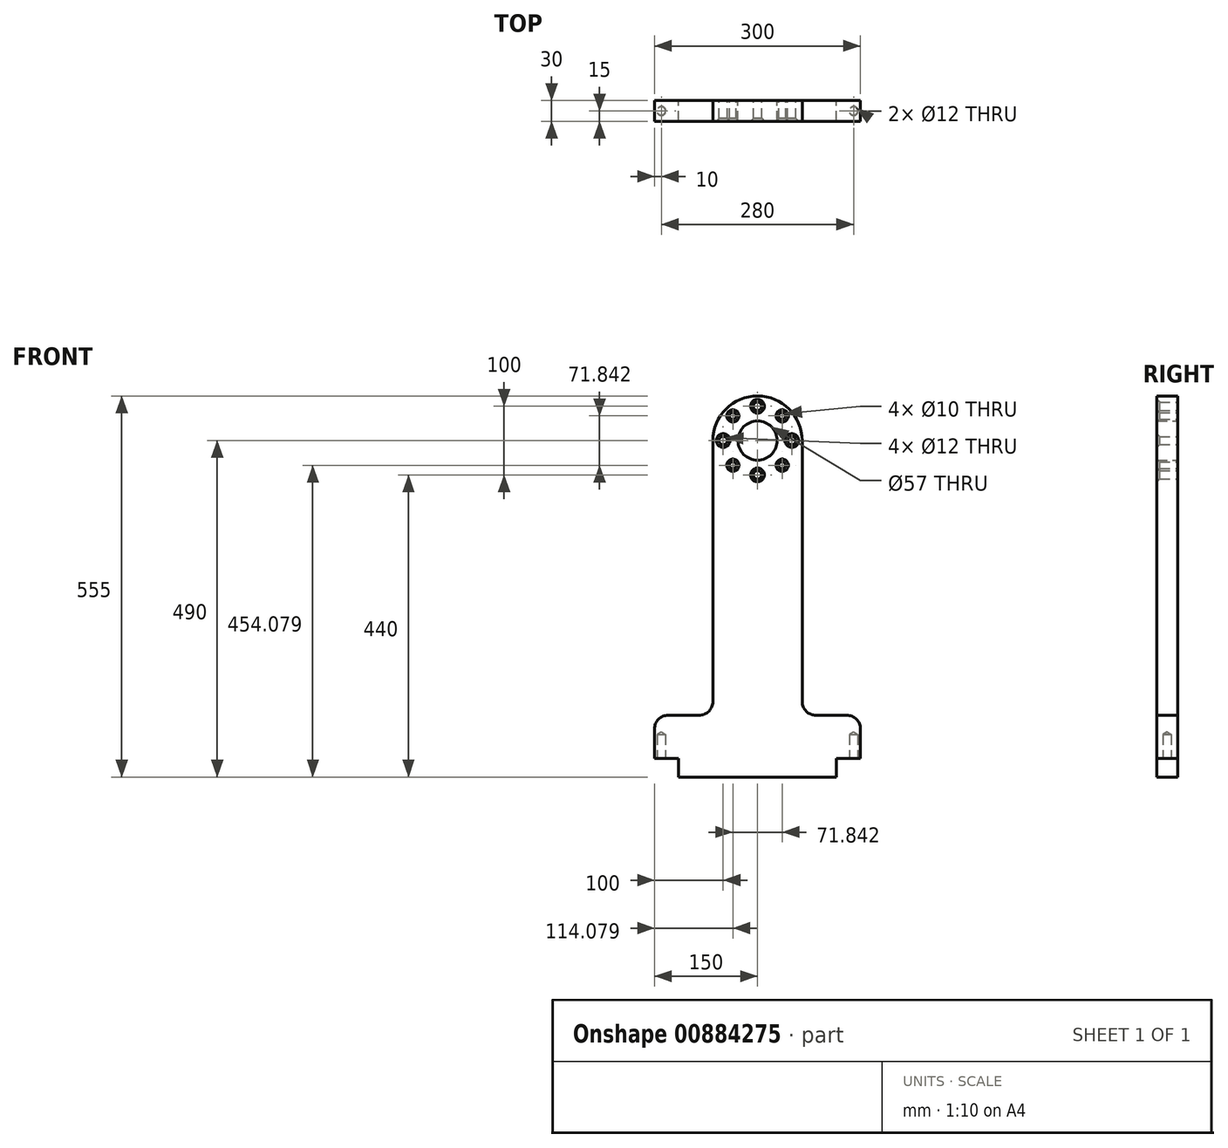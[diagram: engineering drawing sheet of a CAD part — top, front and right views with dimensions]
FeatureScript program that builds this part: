
annotation { "Feature Type Name" : "Feature", "Feature Type Description" : "" }
export const myFeature = defineFeature(function(context is Context, id is Id, definition is map)
    precondition{}
    {
        {
            var Q0;
            Q0=qCreatedBy(makeId("Front.planeOp"),FACE);
            var sketch = newSketch(context, id + "F0", { "sketchPlane" : qUnion([Q0])});
            skLineSegment(sketch, "E0", {"start": v(0, 65) * mm, "end": v(0, 65) * mm});
            skLineSegment(sketch, "E1", {"start": v(65, 0) * mm, "end": v(65, -380) * mm});
            skLineSegment(sketch, "E2", {"start": v(85, -400) * mm, "end": v(130, -400) * mm});
            skLineSegment(sketch, "E3", {"start": v(150, -420) * mm, "end": v(150, -490) * mm});
            skLineSegment(sketch, "E4", {"start": v(150, -490) * mm, "end": v(-150, -490) * mm});
            skLineSegment(sketch, "E5", {"start": v(-150, -490) * mm, "end": v(-150, -420) * mm});
            skLineSegment(sketch, "E6", {"start": v(-130, -400) * mm, "end": v(-85, -400) * mm});
            skLineSegment(sketch, "E7", {"start": v(-65, -380) * mm, "end": v(-65, 0) * mm});
            skPoint(sketch, "E8.visualSharp", {"position": v(-65, 65) * mm});
            skArc(sketch, "E8.filletArc", {"start": v(0, 65) * mm, "mid": v(-45.96, 45.96) * mm, "end": v(-65, 0) * mm});
            skPoint(sketch, "E9.visualSharp", {"position": v(65, 65) * mm});
            skArc(sketch, "E9.filletArc", {"start": v(65, 0) * mm, "mid": v(45.96, 45.96) * mm, "end": v(0, 65) * mm});
            skPoint(sketch, "E10.visualSharp", {"position": v(-65, -400) * mm});
            skArc(sketch, "E10.filletArc", {"start": v(-85, -400) * mm, "mid": v(-70.86, -394.14) * mm, "end": v(-65, -380) * mm});
            skPoint(sketch, "E11.visualSharp", {"position": v(65, -400) * mm});
            skArc(sketch, "E11.filletArc", {"start": v(65, -380) * mm, "mid": v(70.86, -394.14) * mm, "end": v(85, -400) * mm});
            skPoint(sketch, "E12.visualSharp", {"position": v(-150, -400) * mm});
            skArc(sketch, "E12.filletArc", {"start": v(-130, -400) * mm, "mid": v(-144.14, -405.86) * mm, "end": v(-150, -420) * mm});
            skPoint(sketch, "E13.visualSharp", {"position": v(150, -400) * mm});
            skArc(sketch, "E13.filletArc", {"start": v(150, -420) * mm, "mid": v(144.14, -405.86) * mm, "end": v(130, -400) * mm});
            skCircle(sketch, "E14", {"center": v(0, 0) * mm, "radius": 28.5 * mm});
            skCircle(sketch, "E15", {"center": v(0, 50) * mm, "radius": 6 * mm});
            skCircle(sketch, "E16.1.0", {"center": v(-50, 0) * mm, "radius": 6 * mm});
            skCircle(sketch, "E16.2.0", {"center": v(0, -50) * mm, "radius": 6 * mm});
            skCircle(sketch, "E16.3.0", {"center": v(50, 0) * mm, "radius": 6 * mm});
            skCircle(sketch, "E17", {"center": v(-35.92, 35.92) * mm, "radius": 5 * mm});
            skLineSegment(sketch, "E18", {"start": v(-35.92, 35.92) * mm, "end": v(0, 0) * mm, "construction": true});
            skCircle(sketch, "E19.1.0", {"center": v(-35.92, -35.92) * mm, "radius": 5 * mm});
            skCircle(sketch, "E19.2.0", {"center": v(35.92, -35.92) * mm, "radius": 5 * mm});
            skCircle(sketch, "E19.3.0", {"center": v(35.92, 35.92) * mm, "radius": 5 * mm});
            skLineSegment(sketch, "E20.bottom", {"start": v(150, -463) * mm, "end": v(115, -463) * mm});
            skLineSegment(sketch, "E20.top", {"start": v(150, -490) * mm, "end": v(115, -490) * mm});
            skLineSegment(sketch, "E20.left", {"start": v(150, -463) * mm, "end": v(150, -490) * mm});
            skLineSegment(sketch, "E20.right", {"start": v(115, -463) * mm, "end": v(115, -490) * mm});
            skLineSegment(sketch, "E21.bottom", {"start": v(-150, -463) * mm, "end": v(-115, -463) * mm});
            skLineSegment(sketch, "E21.top", {"start": v(-150, -490) * mm, "end": v(-115, -490) * mm});
            skLineSegment(sketch, "E21.left", {"start": v(-150, -463) * mm, "end": v(-150, -490) * mm});
            skLineSegment(sketch, "E21.right", {"start": v(-115, -463) * mm, "end": v(-115, -490) * mm});
            skSolve(sketch);
        }
        {
            var Q0;
            Q0=makeQuery(id+"F0.imprint","IMPRINT",FACE,{"disambiguationData":[TD([[makeQuery(id+"F0.imprint","IMPRINT",EDGE,{"derivedFrom":sQuery(id+"F0.wireOp",EDGE,"E1")}),-1.0]])]});
            extrude(context, id + "F1", {"entities" : qUnion([Q0]), "depth" : 30 * mm, "offsetDistance" : 25 * mm});
        }
        {
            var Q0;
            Q0=makeQuery(id+"F1.opExtrude","CAP_EDGE",EDGE,{"disambiguationData":[OSD([sQuery(id+"F0.wireOp",EDGE,"E17")])],"isStart":false});
            var Q1;
            Q1=makeQuery(id+"F1.opExtrude","CAP_EDGE",EDGE,{"disambiguationData":[OSD([sQuery(id+"F0.wireOp",EDGE,"E15")])],"isStart":false});
            var Q2;
            Q2=makeQuery(id+"F1.opExtrude","CAP_EDGE",EDGE,{"disambiguationData":[OSD([sQuery(id+"F0.wireOp",EDGE,"E19.3.0")])],"isStart":false});
            var Q3;
            Q3=makeQuery(id+"F1.opExtrude","CAP_EDGE",EDGE,{"disambiguationData":[OSD([sQuery(id+"F0.wireOp",EDGE,"E16.3.0")])],"isStart":false});
            var Q4;
            Q4=makeQuery(id+"F1.opExtrude","CAP_EDGE",EDGE,{"disambiguationData":[OSD([sQuery(id+"F0.wireOp",EDGE,"E19.2.0")])],"isStart":false});
            var Q5;
            Q5=makeQuery(id+"F1.opExtrude","CAP_EDGE",EDGE,{"disambiguationData":[OSD([sQuery(id+"F0.wireOp",EDGE,"E16.2.0")])],"isStart":false});
            var Q6;
            Q6=makeQuery(id+"F1.opExtrude","CAP_EDGE",EDGE,{"disambiguationData":[OSD([sQuery(id+"F0.wireOp",EDGE,"E19.1.0")])],"isStart":false});
            var Q7;
            Q7=makeQuery(id+"F1.opExtrude","CAP_EDGE",EDGE,{"disambiguationData":[OSD([sQuery(id+"F0.wireOp",EDGE,"E16.1.0")])],"isStart":false});
            chamfer(context, id + "F2", {"entities" : qUnion([Q0, Q1, Q2, Q3, Q4, Q5, Q6, Q7]), "width" : 4 * mm, "tangentPropagation" : true});
        }
        {
            var Q0;
            Q0=makeQuery(id+"F1.opExtrude","SWEPT_FACE",FACE,{"disambiguationData":[OSD([sQuery(id+"F0.wireOp",EDGE,"E21.bottom")])]});
            var sketch = newSketch(context, id + "F3", { "sketchPlane" : qUnion([Q0])});
            skPoint(sketch, "E22", {"position": v(-140, 15) * mm});
            skPoint(sketch, "E23", {"position": v(140, 15) * mm});
            skSolve(sketch);
        }
        {
            var Q0;
            Q0=sQuery(id+"F3.wireOp",VERTEX,"E22");
            var Q1;
            Q1=sQuery(id+"F3.wireOp",VERTEX,"E23");
            var Q2;
            Q2=makeQuery(id+"F1.opExtrude","SWEPT_BODY",BODY,{"disambiguationData":[OSD([sQuery(id+"F0.wireOp",EDGE,"E1"),sQuery(id+"F0.wireOp",EDGE,"E2"),sQuery(id+"F0.wireOp",EDGE,"E3"),sQuery(id+"F0.wireOp",EDGE,"E4"),sQuery(id+"F0.wireOp",EDGE,"E5"),sQuery(id+"F0.wireOp",EDGE,"E6"),sQuery(id+"F0.wireOp",EDGE,"E7"),sQuery(id+"F0.wireOp",EDGE,"E8.filletArc"),sQuery(id+"F0.wireOp",EDGE,"E9.filletArc"),sQuery(id+"F0.wireOp",EDGE,"E10.filletArc"),sQuery(id+"F0.wireOp",EDGE,"E11.filletArc"),sQuery(id+"F0.wireOp",EDGE,"E12.filletArc"),sQuery(id+"F0.wireOp",EDGE,"E13.filletArc"),sQuery(id+"F0.wireOp",EDGE,"E14"),sQuery(id+"F0.wireOp",EDGE,"E15"),sQuery(id+"F0.wireOp",EDGE,"E16.1.0"),sQuery(id+"F0.wireOp",EDGE,"E16.2.0"),sQuery(id+"F0.wireOp",EDGE,"E16.3.0"),sQuery(id+"F0.wireOp",EDGE,"E17"),sQuery(id+"F0.wireOp",EDGE,"E19.1.0"),sQuery(id+"F0.wireOp",EDGE,"E19.2.0"),sQuery(id+"F0.wireOp",EDGE,"E19.3.0"),sQuery(id+"F0.wireOp",EDGE,"E20.bottom"),sQuery(id+"F0.wireOp",EDGE,"E20.right"),sQuery(id+"F0.wireOp",EDGE,"E21.bottom"),sQuery(id+"F0.wireOp",EDGE,"E21.right")])]});
            hole(context, id + "F4", {"style" : HoleStyle.C_SINK, "endStyle" : HoleEndStyle.BLIND, "holeDiameter" : 12 * mm, "cSinkDiameter" : 13 * mm, "cSinkAngle" : 90 * degree, "majorDiameter" : 5 * mm, "holeDepth" : 35 * mm, "tappedDepth" : 26.25 * mm, "tapClearance" : 3, "startFromSketch" : true, "locations" : qUnion([Q0, Q1]), "scope" : qUnion([Q2])});
        }
    });
